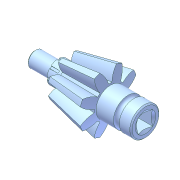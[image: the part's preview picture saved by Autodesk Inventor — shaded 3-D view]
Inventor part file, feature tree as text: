
AUTODESK INVENTOR PART (.ipt)
format: ipt  version: 2016 (Build 200138000, 138)  size: 289,280 bytes
history: native  units: in
note: dims shown in document units (in); Inventor stores cm internally (conversion verified against a paired STEP export)
features: sketch x10, extrude x6, plane x3, chamfer x3, revolve x2, other x1, loft x1, pattern_circular x1
ambient origin geometry x8: Origin, YZ Plane, XZ Plane, XY Plane, X Axis, Y Axis, Z Axis, Center Point
bodies: Solid1 (feature_tree)
feature tree (27):
  revolve  "Revolution1"  [1 undecoded]
  other  "Work Point1"
  plane  "Work Plane7"
  sketch  "Sketch12"  dims[d10=90.0deg d88=0.1575in]
  extrude  "Extrusion8"  Depth=0.1575in
  extrude  "Extrusion9"  Depth=0.065in
  extrude  "Extrusion10"  Depth=0.0492in
  revolve  "Revolution3"  [1 undecoded]
  extrude  "Extrusion11"  Depth=0.315in
  chamfer  "Chamfer3"  Distance=0.2362in
  extrude  "Extrusion12"  Depth=0.1575in TaperAngle=0.0deg
  chamfer  "Chamfer4"  Angle=90.0deg  [1 undecoded]
  plane  "Work Plane9"
  loft  "Loft1"
  pattern_circular  "Circular Pattern3"  [2 undecoded]
  extrude  "Extrusion13"  Depth=0.0197in TaperAngle=30.0deg
  chamfer  "Chamfer5"  Distance=0.1181in
  sketch  "Sketch1"  dims[d1=0.1825in d2=0.0394in]
  sketch  "Sketch14"  dims[d89=0.0812in d90=0.065in]
  sketch  "Sketch15"  dims[d91=0.2756in d92=0.0492in]
  sketch  "Sketch16"  dims[d93=0.0984in d94=0.2756in]
  sketch  "Sketch17"  dims[d96=0.9449in d97=0.315in]
  sketch  "Sketch18"  dims[d98=0.9449in d99=0.2362in d100=0.0in]
  sketch  "Sketch19"  dims[d101=0.0787in d102=0.0in d103=0.1575in d104=0.0in]
  plane  "Work Plane8"
  sketch  "Sketch20"  dims[d105=0.0394in]
  sketch  "Sketch21"  dims[d106=0.0984in d107=90.0deg d108=0.0984in d109=0.1181in d110=0.0in d111=0.0197in d112=0.0787in d113=30.0deg d115=0.1181in d116=0.0in d117=0.0079in d118=0.0787in d119=30.0deg d120=0.0079in d121=0.0787in d122=30.0deg d123=0.0in d124=0.9579in d125=0.065in d126=0.9646in d127=0.0394in d128=0.0886in d129=0.0309in d131=0.0098in d132=0.0in d133=90.0deg d134=0.0in d135=90.0deg d136=3.1496in d137=360.0deg d139=0.0787in d140=0.1575in d141=0.0in d142=0.0984in d143=0.0in d144=0.0in]
note: 5 required parameter values undecoded (feature->parameter linkage not recoverable at this tier; creation-order binding heuristic only, values carry confidence <= 0.55)